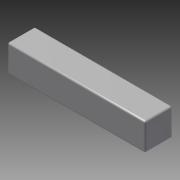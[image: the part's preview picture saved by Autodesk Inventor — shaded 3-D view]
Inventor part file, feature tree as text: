
AUTODESK INVENTOR PART (.ipt)
format: ipt  version: 2014 (Build 180170000, 170)  size: 115,712 bytes
history: native  units: mm (DEFAULTED — no unit token found)
features: other x2, sketch x1, fillet x1
ambient origin geometry x8: Origin, YZ Plane, XZ Plane, XY Plane, X Axis, Y Axis, Z Axis, Center Point
bodies: Solid1 (feature_tree), Body1 (feature_tree)
feature tree (4):
  sketch  "Sketch1"  dims[d1=10.0mm d2=-1.5875mm d3=0.4125mm d4=10.0mm d5=0.0mm d9=0.0mm d10=0.0mm d11=0.0mm d12=0.0mm d13=0.127mm]
  other  "IDS_WORKPLANE{1}"
  other  "IDS_WORKPLANE{2}"
  fillet  "Fillet1"  Radius=1.0mm
